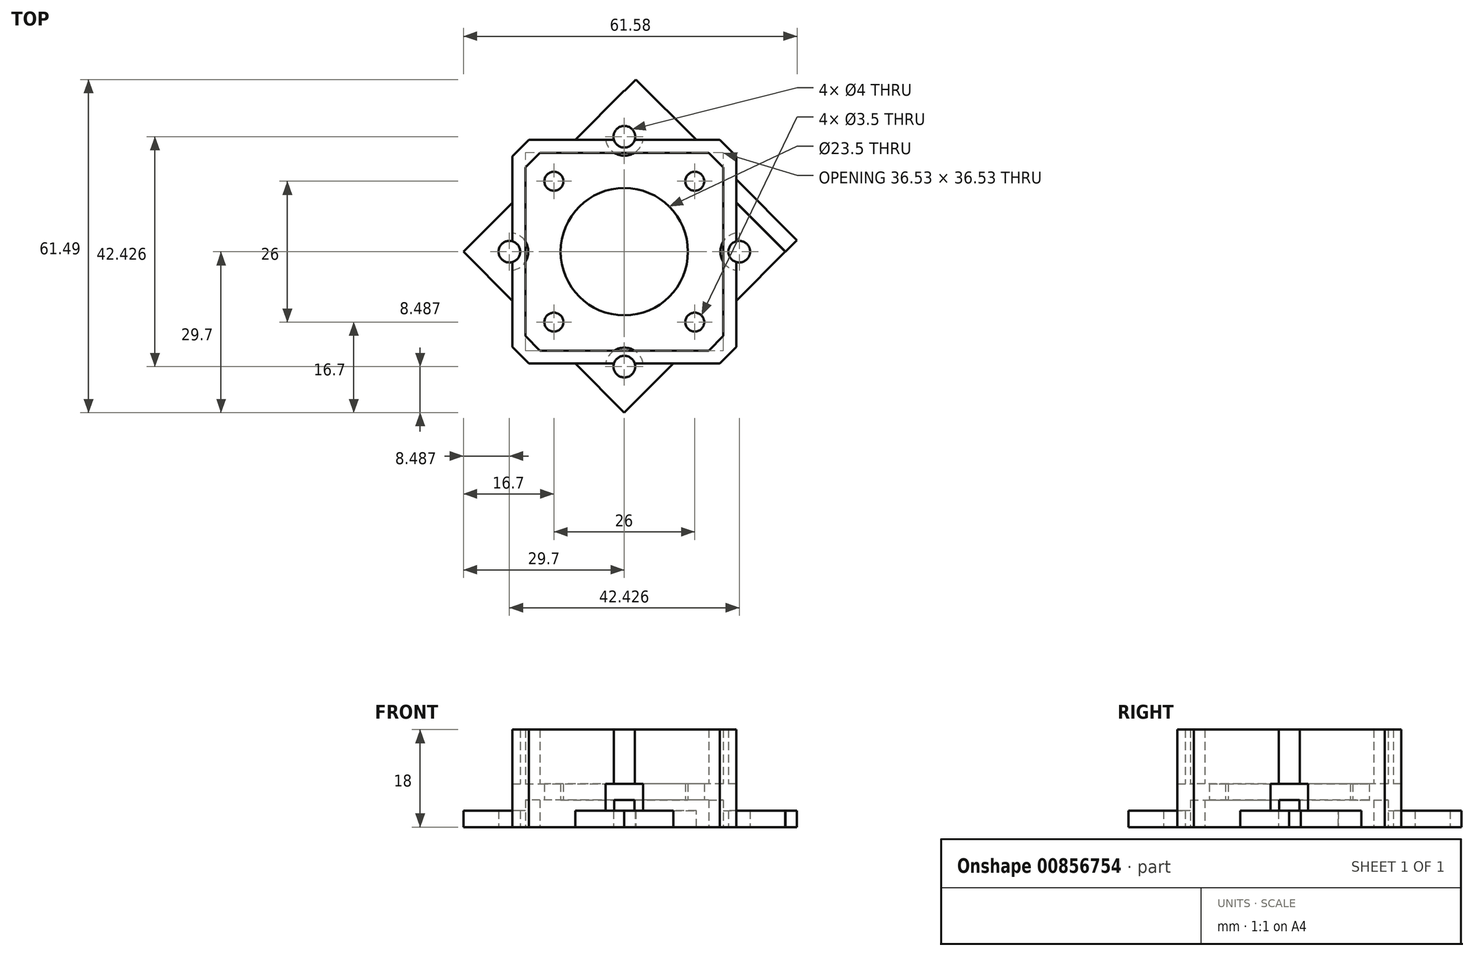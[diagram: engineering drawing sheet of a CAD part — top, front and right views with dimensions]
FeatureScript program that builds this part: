
annotation { "Feature Type Name" : "Feature", "Feature Type Description" : "" }
export const myFeature = defineFeature(function(context is Context, id is Id, definition is map)
    precondition{}
    {
        {
            var Q0;
            Q0=qCreatedBy(makeId("Top.planeOp"),FACE);
            var sketch = newSketch(context, id + "F0", { "sketchPlane" : qUnion([Q0])});
            skLineSegment(sketch, "E0", {"start": v(0, 0) * mm, "end": v(-17.6, 15) * mm});
            skLineSegment(sketch, "E1", {"start": v(0, 0) * mm, "end": v(-15, 17.6) * mm});
            skLineSegment(sketch, "E2", {"start": v(0, 0) * mm, "end": v(-17.6, -15) * mm});
            skLineSegment(sketch, "E3", {"start": v(0, 0) * mm, "end": v(-15, -17.6) * mm});
            skLineSegment(sketch, "E4", {"start": v(0, 0) * mm, "end": v(15, 17.6) * mm});
            skLineSegment(sketch, "E5", {"start": v(0, 0) * mm, "end": v(17.6, 15) * mm});
            skLineSegment(sketch, "E6", {"start": v(0, 0) * mm, "end": v(15, -17.6) * mm});
            skLineSegment(sketch, "E7", {"start": v(0, 0) * mm, "end": v(17.6, -15) * mm});
            skLineSegment(sketch, "E8", {"start": v(0, 0) * mm, "end": v(15.57, 18.27) * mm});
            skLineSegment(sketch, "E9", {"start": v(0, 0) * mm, "end": v(18.27, 15.57) * mm});
            skLineSegment(sketch, "E10", {"start": v(0, 0) * mm, "end": v(18.27, -15.57) * mm});
            skLineSegment(sketch, "E11", {"start": v(0, 0) * mm, "end": v(15.57, -18.27) * mm});
            skLineSegment(sketch, "E12", {"start": v(0, 0) * mm, "end": v(-15.57, -18.27) * mm});
            skLineSegment(sketch, "E13", {"start": v(0, 0) * mm, "end": v(-18.27, -15.57) * mm});
            skLineSegment(sketch, "E14", {"start": v(0, 0) * mm, "end": v(-15.57, 18.27) * mm});
            skLineSegment(sketch, "E15", {"start": v(0, 0) * mm, "end": v(-18.27, 15.57) * mm});
            skLineSegment(sketch, "E16", {"start": v(0, 0) * mm, "end": v(17.6, 20.65) * mm});
            skLineSegment(sketch, "E17", {"start": v(17.6, 20.65) * mm, "end": v(0, 0) * mm});
            skLineSegment(sketch, "E18", {"start": v(0, 0) * mm, "end": v(20.65, 17.6) * mm});
            skLineSegment(sketch, "E19", {"start": v(0, 0) * mm, "end": v(20.65, -17.6) * mm});
            skLineSegment(sketch, "E20", {"start": v(0, 0) * mm, "end": v(17.6, -20.65) * mm});
            skLineSegment(sketch, "E21", {"start": v(0, 0) * mm, "end": v(-17.6, -20.65) * mm});
            skLineSegment(sketch, "E22", {"start": v(0, 0) * mm, "end": v(-20.65, -17.6) * mm});
            skLineSegment(sketch, "E23", {"start": v(0, 0) * mm, "end": v(-20.65, 17.6) * mm});
            skLineSegment(sketch, "E24", {"start": v(0, 0) * mm, "end": v(-17.6, 20.65) * mm});
            skSolve(sketch);
        }
        {
            var Q0;
            Q0=qCreatedBy(makeId("Top.planeOp"),FACE);
            var sketch = newSketch(context, id + "F1", { "sketchPlane" : qUnion([Q0])});
            skLineSegment(sketch, "E25", {"start": v(-18.27, -15.57) * mm, "end": v(-18.27, 15.57) * mm});
            skLineSegment(sketch, "E26", {"start": v(-18.27, 15.57) * mm, "end": v(-15.57, 18.27) * mm});
            skLineSegment(sketch, "E27", {"start": v(-15.57, 18.27) * mm, "end": v(15.57, 18.27) * mm});
            skLineSegment(sketch, "E28", {"start": v(15.57, 18.27) * mm, "end": v(18.27, 15.57) * mm});
            skLineSegment(sketch, "E29", {"start": v(18.27, 15.57) * mm, "end": v(18.27, -15.57) * mm});
            skLineSegment(sketch, "E30", {"start": v(18.27, -15.57) * mm, "end": v(15.57, -18.27) * mm});
            skLineSegment(sketch, "E31", {"start": v(15.57, -18.27) * mm, "end": v(-15.57, -18.27) * mm});
            skLineSegment(sketch, "E32", {"start": v(-15.57, -18.27) * mm, "end": v(-18.27, -15.57) * mm});
            skLineSegment(sketch, "E33", {"start": v(-20.65, 17.6) * mm, "end": v(-20.65, -17.6) * mm});
            skLineSegment(sketch, "E34", {"start": v(-20.65, -17.6) * mm, "end": v(-17.6, -20.65) * mm});
            skLineSegment(sketch, "E35", {"start": v(-17.6, -20.65) * mm, "end": v(17.6, -20.65) * mm});
            skLineSegment(sketch, "E36", {"start": v(17.6, -20.65) * mm, "end": v(20.65, -17.6) * mm});
            skLineSegment(sketch, "E37", {"start": v(20.65, -17.6) * mm, "end": v(20.65, 17.6) * mm});
            skLineSegment(sketch, "E38", {"start": v(20.65, 17.6) * mm, "end": v(17.6, 20.65) * mm});
            skLineSegment(sketch, "E39", {"start": v(17.6, 20.65) * mm, "end": v(-17.6, 20.65) * mm});
            skLineSegment(sketch, "E40", {"start": v(-17.6, 20.65) * mm, "end": v(-20.65, 17.6) * mm});
            skSolve(sketch);
        }
        {
            var Q0;
            Q0=qCreatedBy(makeId("Top.planeOp"),FACE);
            var sketch = newSketch(context, id + "F2", { "sketchPlane" : qUnion([Q0])});
            skCircle(sketch, "E41", {"center": v(0, 0) * mm, "radius": 11.75 * mm});
            skCircle(sketch, "E42", {"center": v(13, 13) * mm, "radius": 1.75 * mm});
            skCircle(sketch, "E43.MirrorC", {"center": v(-13, -13) * mm, "radius": 1.75 * mm});
            skCircle(sketch, "E44.MirrorC", {"center": v(13, -13) * mm, "radius": 1.75 * mm});
            skLineSegment(sketch, "E45", {"start": v(-18.27, 15.57) * mm, "end": v(-15.57, 18.27) * mm});
            skLineSegment(sketch, "E46", {"start": v(-15.57, 18.27) * mm, "end": v(15.57, 18.27) * mm});
            skLineSegment(sketch, "E47", {"start": v(15.57, 18.27) * mm, "end": v(18.27, 15.57) * mm});
            skLineSegment(sketch, "E48", {"start": v(18.27, 15.57) * mm, "end": v(18.27, -15.57) * mm});
            skLineSegment(sketch, "E49", {"start": v(18.27, -15.57) * mm, "end": v(15.57, -18.27) * mm});
            skLineSegment(sketch, "E50", {"start": v(15.57, -18.27) * mm, "end": v(-15.57, -18.27) * mm});
            skLineSegment(sketch, "E51", {"start": v(-15.57, -18.27) * mm, "end": v(-18.27, -15.57) * mm});
            skLineSegment(sketch, "E52", {"start": v(-18.27, -15.57) * mm, "end": v(-18.27, 15.57) * mm});
            skCircle(sketch, "E53.MirrorC", {"center": v(-13, 13) * mm, "radius": 1.75 * mm});
            skSolve(sketch);
        }
        {
            var Q0;
            Q0=qCreatedBy(makeId("Top.planeOp"),FACE);
            var sketch = newSketch(context, id + "F3", { "sketchPlane" : qUnion([Q0])});
            skLineSegment(sketch, "E54.bottom", {"start": v(0, -29.7) * mm, "end": v(-29.7, 0) * mm});
            skLineSegment(sketch, "E54.top", {"start": v(29.7, 0) * mm, "end": v(0, 29.7) * mm});
            skLineSegment(sketch, "E54.left", {"start": v(0, -29.7) * mm, "end": v(29.7, 0) * mm});
            skLineSegment(sketch, "E54.right", {"start": v(-29.7, 0) * mm, "end": v(0, 29.7) * mm});
            skPoint(sketch, "E54.middle", {"position": v(0, 0) * mm});
            skCircle(sketch, "E55", {"center": v(0, 0) * mm, "radius": 11.75 * mm});
            skCircle(sketch, "E56", {"center": v(0, 21.21) * mm, "radius": 2 * mm});
            skCircle(sketch, "E57", {"center": v(21.21, 0) * mm, "radius": 2 * mm});
            skCircle(sketch, "E58", {"center": v(-21.21, 0) * mm, "radius": 2 * mm});
            skCircle(sketch, "E59", {"center": v(0, -21.21) * mm, "radius": 2 * mm});
            skLineSegment(sketch, "E60.bottom", {"start": v(0, 21.21) * mm, "end": v(21.21, 0) * mm, "construction": true});
            skLineSegment(sketch, "E60.top", {"start": v(-21.21, 0) * mm, "end": v(0, -21.21) * mm, "construction": true});
            skLineSegment(sketch, "E60.left", {"start": v(0, 21.21) * mm, "end": v(-21.21, 0) * mm, "construction": true});
            skLineSegment(sketch, "E60.right", {"start": v(21.21, 0) * mm, "end": v(0, -21.21) * mm, "construction": true});
            skCircle(sketch, "E61", {"center": v(-13, 13) * mm, "radius": 1.75 * mm});
            skCircle(sketch, "E62", {"center": v(-13, -13) * mm, "radius": 1.75 * mm});
            skCircle(sketch, "E63", {"center": v(13, -13) * mm, "radius": 1.75 * mm});
            skCircle(sketch, "E64", {"center": v(13, 13) * mm, "radius": 1.75 * mm});
            skSolve(sketch);
        }
        {
            var Q0;
            Q0=makeQuery(id+"F1.imprint","IMPRINT",FACE,{"disambiguationData":[TD([[makeQuery(id+"F1.imprint","IMPRINT",EDGE,{"derivedFrom":sQuery(id+"F1.wireOp",EDGE,"E25")}),1.0]])]});
            extrude(context, id + "F4", {"entities" : qUnion([Q0]), "depth" : 18 * mm, "offsetDistance" : 25 * mm});
        }
        {
            var Q0;
            Q0=makeQuery(id+"F2.imprint","IMPRINT",FACE,{"disambiguationData":[TD([[makeQuery(id+"F2.imprint","IMPRINT",EDGE,{"derivedFrom":sQuery(id+"F2.wireOp",EDGE,"E41")}),-1.0]])]});
            extrude(context, id + "F5", {"entities" : qUnion([Q0]), "operationType" : NewBodyOperationType.ADD, "depth" : 8 * mm, "offsetDistance" : 25 * mm});
        }
        {
            var Q0;
            Q0=makeQuery(id+"F3.imprint","IMPRINT",FACE,{"disambiguationData":[TD([[makeQuery(id+"F3.imprint","IMPRINT",EDGE,{"derivedFrom":sQuery(id+"F3.wireOp",EDGE,"E54.bottom")}),-1.0]])]});
            extrude(context, id + "F6", {"entities" : qUnion([Q0]), "operationType" : NewBodyOperationType.ADD, "depth" : 3 * mm, "offsetDistance" : 25 * mm});
        }
        {
            var Q0;
            Q0=makeQuery(id+"F3.imprint","IMPRINT",FACE,{"disambiguationData":[TD([[makeQuery(id+"F3.imprint","IMPRINT",EDGE,{"derivedFrom":sQuery(id+"F3.wireOp",EDGE,"E57")}),1.0]])]});
            var Q1;
            Q1=makeQuery(id+"F3.imprint","IMPRINT",FACE,{"disambiguationData":[TD([[makeQuery(id+"F3.imprint","IMPRINT",EDGE,{"derivedFrom":sQuery(id+"F3.wireOp",EDGE,"E56")}),1.0]])]});
            var Q2;
            Q2=makeQuery(id+"F3.imprint","IMPRINT",FACE,{"disambiguationData":[TD([[makeQuery(id+"F3.imprint","IMPRINT",EDGE,{"derivedFrom":sQuery(id+"F3.wireOp",EDGE,"E59")}),1.0]])]});
            var Q3;
            Q3=makeQuery(id+"F3.imprint","IMPRINT",FACE,{"disambiguationData":[TD([[makeQuery(id+"F3.imprint","IMPRINT",EDGE,{"derivedFrom":sQuery(id+"F3.wireOp",EDGE,"E58")}),1.0]])]});
            extrude(context, id + "F7", {"entities" : qUnion([Q0, Q1, Q2, Q3]), "operationType" : NewBodyOperationType.REMOVE, "oppositeDirection" : true, "depth" : -18 * mm, "offsetDistance" : 25 * mm});
        }
        {
            var Q0;
            Q0=makeQuery(id+"F6.boolean.opBoolean","MERGE",FACE,{"derivedFrom":[makeQuery(id+"F5.boolean.opBoolean","MERGE",FACE,{"derivedFrom":[makeQuery(id+"F4.opExtrude","CAP_FACE",FACE,{"disambiguationData":[OSD([sQuery(id+"F1.wireOp",EDGE,"E25"),sQuery(id+"F1.wireOp",EDGE,"E26"),sQuery(id+"F1.wireOp",EDGE,"E27"),sQuery(id+"F1.wireOp",EDGE,"E28"),sQuery(id+"F1.wireOp",EDGE,"E29"),sQuery(id+"F1.wireOp",EDGE,"E30"),sQuery(id+"F1.wireOp",EDGE,"E31"),sQuery(id+"F1.wireOp",EDGE,"E32"),sQuery(id+"F1.wireOp",EDGE,"E33"),sQuery(id+"F1.wireOp",EDGE,"E34"),sQuery(id+"F1.wireOp",EDGE,"E35"),sQuery(id+"F1.wireOp",EDGE,"E36"),sQuery(id+"F1.wireOp",EDGE,"E37"),sQuery(id+"F1.wireOp",EDGE,"E38"),sQuery(id+"F1.wireOp",EDGE,"E39"),sQuery(id+"F1.wireOp",EDGE,"E40")])],"isStart":true}),makeQuery(id+"F5.opExtrude","CAP_FACE",FACE,{"disambiguationData":[OSD([sQuery(id+"F2.wireOp",EDGE,"E41"),sQuery(id+"F2.wireOp",EDGE,"E42"),sQuery(id+"F2.wireOp",EDGE,"E43.MirrorC"),sQuery(id+"F2.wireOp",EDGE,"E44.MirrorC"),sQuery(id+"F2.wireOp",EDGE,"E45"),sQuery(id+"F2.wireOp",EDGE,"E46"),sQuery(id+"F2.wireOp",EDGE,"E47"),sQuery(id+"F2.wireOp",EDGE,"E48"),sQuery(id+"F2.wireOp",EDGE,"E49"),sQuery(id+"F2.wireOp",EDGE,"E50"),sQuery(id+"F2.wireOp",EDGE,"E51"),sQuery(id+"F2.wireOp",EDGE,"E52"),sQuery(id+"F2.wireOp",EDGE,"E53.MirrorC")])],"isStart":true})]}),makeQuery(id+"F6.opExtrude","CAP_FACE",FACE,{"disambiguationData":[OSD([sQuery(id+"F3.wireOp",EDGE,"E54.bottom"),sQuery(id+"F3.wireOp",EDGE,"E54.top"),sQuery(id+"F3.wireOp",EDGE,"E54.left"),sQuery(id+"F3.wireOp",EDGE,"E54.right"),sQuery(id+"F3.wireOp",EDGE,"E55"),sQuery(id+"F3.wireOp",EDGE,"E56"),sQuery(id+"F3.wireOp",EDGE,"E57"),sQuery(id+"F3.wireOp",EDGE,"E58"),sQuery(id+"F3.wireOp",EDGE,"E59"),sQuery(id+"F3.wireOp",EDGE,"E61"),sQuery(id+"F3.wireOp",EDGE,"E62"),sQuery(id+"F3.wireOp",EDGE,"E63"),sQuery(id+"F3.wireOp",EDGE,"E64")])],"isStart":true})]});
            var sketch = newSketch(context, id + "F8", { "sketchPlane" : qUnion([Q0])});
            skCircle(sketch, "E65", {"center": v(13, 13) * mm, "radius": 4.5 * mm});
            skCircle(sketch, "E66", {"center": v(-13, -13) * mm, "radius": 4.5 * mm});
            skCircle(sketch, "E67", {"center": v(13, -13) * mm, "radius": 4.5 * mm});
            skCircle(sketch, "E68", {"center": v(-13, 13) * mm, "radius": 4.5 * mm});
            skSolve(sketch);
        }
        {
            var Q0;
            Q0=makeQuery(id+"F8.imprint","IMPRINT",FACE,{"disambiguationData":[TD([[makeQuery(id+"F8.imprint","IMPRINT",EDGE,{"derivedFrom":sQuery(id+"F8.wireOp",EDGE,"E66")}),1.0]])]});
            var Q1;
            Q1=makeQuery(id+"F2.imprint","IMPRINT",FACE,{"disambiguationData":[TD([[makeQuery(id+"F2.imprint","IMPRINT",EDGE,{"derivedFrom":sQuery(id+"F2.wireOp",EDGE,"E53.MirrorC")}),-1.0]])]});
            extrude(context, id + "F9", {"entities" : qUnion([Q0, Q1]), "operationType" : NewBodyOperationType.REMOVE, "oppositeDirection" : true, "depth" : 5 * mm, "offsetDistance" : 25 * mm});
        }
        {
            var Q0;
            Q0=makeQuery(id+"F8.imprint","IMPRINT",FACE,{"disambiguationData":[TD([[makeQuery(id+"F8.imprint","IMPRINT",EDGE,{"derivedFrom":sQuery(id+"F8.wireOp",EDGE,"E65")}),1.0]])]});
            var Q1;
            Q1=makeQuery(id+"F2.imprint","IMPRINT",FACE,{"disambiguationData":[TD([[makeQuery(id+"F2.imprint","IMPRINT",EDGE,{"derivedFrom":sQuery(id+"F2.wireOp",EDGE,"E44.MirrorC")}),-1.0]])]});
            extrude(context, id + "F10", {"entities" : qUnion([Q0, Q1]), "operationType" : NewBodyOperationType.REMOVE, "oppositeDirection" : true, "depth" : 5 * mm, "offsetDistance" : 25 * mm});
        }
        {
            var Q0;
            {var subQ0=sQuery(id+"F3.wireOp",EDGE,"E54.top");var subQ1=sQuery(id+"F3.wireOp",EDGE,"E54.right");var subQ2=sQuery(id+"F3.wireOp",EDGE,"E56");Q0=makeQuery(id+"F6.boolean.opBoolean","SPLIT",FACE,{"disambiguationData":[TD([makeQuery(id+"F4.opExtrude","SWEPT_FACE",FACE,{"disambiguationData":[OSD([sQuery(id+"F1.wireOp",EDGE,"E39")])]})])],"derivedFrom":makeQuery(id+"F6.opExtrude","CAP_FACE",FACE,{"disambiguationData":[OSD([sQuery(id+"F3.wireOp",EDGE,"E54.bottom"),subQ0,sQuery(id+"F3.wireOp",EDGE,"E54.left"),subQ1,sQuery(id+"F3.wireOp",EDGE,"E55"),subQ2,sQuery(id+"F3.wireOp",EDGE,"E57"),sQuery(id+"F3.wireOp",EDGE,"E58"),sQuery(id+"F3.wireOp",EDGE,"E59"),sQuery(id+"F3.wireOp",EDGE,"E61"),sQuery(id+"F3.wireOp",EDGE,"E62"),sQuery(id+"F3.wireOp",EDGE,"E63"),sQuery(id+"F3.wireOp",EDGE,"E64")])],"isStart":false})});}
            var sketch = newSketch(context, id + "F11", { "sketchPlane" : qUnion([Q0])});
            skCircle(sketch, "E69", {"center": v(0, 21.21) * mm, "radius": 3.5 * mm});
            skCircle(sketch, "E70", {"center": v(0, -21.21) * mm, "radius": 3.5 * mm});
            skCircle(sketch, "E71", {"center": v(21.21, 0) * mm, "radius": 3.5 * mm});
            skCircle(sketch, "E72", {"center": v(-21.21, 0) * mm, "radius": 3.5 * mm});
            skSolve(sketch);
        }
        {
            var Q0;
            Q0 = qSketchRegion(id + "F11", true);
            extrude(context, id + "F12", {"entities" : qUnion([Q0]), "operationType" : NewBodyOperationType.REMOVE, "oppositeDirection" : true, "depth" : -5 * mm, "offsetDistance" : 25 * mm});
        }
        {
            var Q0;
            Q0=makeQuery(id+"F3.imprint","IMPRINT",FACE,{"disambiguationData":[TD([[makeQuery(id+"F3.imprint","IMPRINT",EDGE,{"derivedFrom":sQuery(id+"F3.wireOp",EDGE,"E54.bottom")}),-1.0]])]});
            var sketch = newSketch(context, id + "F13", { "sketchPlane" : qUnion([Q0])});
            skLineSegment(sketch, "E73", {"start": v(0, 29.64) * mm, "end": v(4.3, 33.94) * mm});
            skLineSegment(sketch, "E74", {"start": v(29.75, 0) * mm, "end": v(34, 4.25) * mm});
            skLineSegment(sketch, "E75", {"start": v(17.6, 20.65) * mm, "end": v(4.3, 33.94) * mm});
            skLineSegment(sketch, "E76", {"start": v(20.65, 17.6) * mm, "end": v(34, 4.25) * mm});
            skLineSegment(sketch, "E77", {"start": v(2.15, 31.79) * mm, "end": v(31.88, 2.12) * mm});
            skLineSegment(sketch, "E78", {"start": v(0, 29.64) * mm, "end": v(29.75, 0) * mm});
            skLineSegment(sketch, "E79", {"start": v(13.46, 20.5) * mm, "end": v(9.17, 20.5) * mm});
            skLineSegment(sketch, "E80", {"start": v(20.48, 13.5) * mm, "end": v(20.48, 9.24) * mm});
            skLineSegment(sketch, "E81", {"start": v(13.46, 20.5) * mm, "end": v(17.6, 20.65) * mm});
            skLineSegment(sketch, "E82", {"start": v(20.48, 13.5) * mm, "end": v(20.65, 17.6) * mm});
            skLineSegment(sketch, "E83", {"start": v(20.65, 17.6) * mm, "end": v(45.4, -7.15) * mm});
            skLineSegment(sketch, "E84", {"start": v(17.6, 20.65) * mm, "end": v(-7.15, 45.4) * mm});
            skLineSegment(sketch, "E85", {"start": v(-7.15, 45.4) * mm, "end": v(-9.3, 43.24) * mm});
            skLineSegment(sketch, "E86", {"start": v(2.15, 31.79) * mm, "end": v(-9.3, 43.24) * mm});
            skLineSegment(sketch, "E87", {"start": v(31.88, 2.12) * mm, "end": v(43.27, -9.27) * mm});
            skLineSegment(sketch, "E88", {"start": v(45.4, -7.15) * mm, "end": v(43.27, -9.27) * mm});
            skSolve(sketch);
        }
        {
            var Q0;
            {var subQ0=sQuery(id+"F13.wireOp",EDGE,"E77");var subQ1=sQuery(id+"F13.wireOp",EDGE,"E73");var subQ2=makeQuery(id+"F13.imprint","INTERSECT",VERTEX,{"derivedFrom":[subQ1,subQ0]});Q0=makeQuery(id+"F13.imprint","IMPRINT",FACE,{"disambiguationData":[TD([[makeQuery(id+"F13.imprint","IMPRINT",EDGE,{"disambiguationData":[TD([[subQ2,1.0]])],"derivedFrom":subQ1}),-1.0]])]});}
            var Q1;
            {var subQ5=sQuery(id+"F13.wireOp",EDGE,"E80");Q1=makeQuery(id+"F13.imprint","IMPRINT",FACE,{"disambiguationData":[TD([[makeQuery(id+"F13.imprint","IMPRINT",EDGE,{"derivedFrom":subQ5}),1.0]])]});}
            extrude(context, id + "F14", {"entities" : qUnion([Q0, Q1]), "operationType" : NewBodyOperationType.ADD, "depth" : 3 * mm, "offsetDistance" : 25 * mm});
        }
        {
            var Q0;
            Q0=makeQuery(id+"F8.imprint","IMPRINT",FACE,{"disambiguationData":[TD([[makeQuery(id+"F8.imprint","IMPRINT",EDGE,{"derivedFrom":sQuery(id+"F8.wireOp",EDGE,"E67")}),1.0]])]});
            extrude(context, id + "F15", {"entities" : qUnion([Q0]), "operationType" : NewBodyOperationType.REMOVE, "oppositeDirection" : true, "depth" : 5 * mm, "offsetDistance" : 25 * mm});
        }
        {
            var Q0;
            Q0=makeQuery(id+"F8.imprint","IMPRINT",FACE,{"disambiguationData":[TD([[makeQuery(id+"F8.imprint","IMPRINT",EDGE,{"derivedFrom":sQuery(id+"F8.wireOp",EDGE,"E68")}),1.0]])]});
            extrude(context, id + "F16", {"entities" : qUnion([Q0]), "operationType" : NewBodyOperationType.REMOVE, "oppositeDirection" : true, "depth" : 5 * mm, "offsetDistance" : 25 * mm});
        }
        {
            var Q0;
            Q0=makeQuery(id+"FBqxjdhl6pFCTmG_1.boolean.opBoolean","MERGE",FACE,{"derivedFrom":[makeQuery(id+"F4.opExtrude","SWEPT_FACE",FACE,{"disambiguationData":[OSD([sQuery(id+"F1.wireOp",EDGE,"E38")])]}),makeQuery(id+"FBqxjdhl6pFCTmG_1.opExtrude","SWEPT_FACE",FACE,{"disambiguationData":[OSD([sQuery(id+"F13.wireOp",EDGE,"E83")])]}),makeQuery(id+"FBqxjdhl6pFCTmG_1.opExtrude","SWEPT_FACE",FACE,{"disambiguationData":[OSD([sQuery(id+"F13.wireOp",EDGE,"E84")])]})]});
            var sketch = newSketch(context, id + "F17", { "sketchPlane" : qUnion([Q0])});
            skLineSegment(sketch, "E89", {"start": v(37.16, 3.2) * mm, "end": v(33.16, 3.2) * mm});
            skCircle(sketch, "E90", {"center": v(33.16, 3.2) * mm, "radius": 1.75 * mm});
            skLineSegment(sketch, "E91", {"start": v(0, 0) * mm, "end": v(0, 18) * mm});
            skLineSegment(sketch, "E92", {"start": v(37.16, 10) * mm, "end": v(-37.16, 10) * mm});
            skCircle(sketch, "E93.MirrorC", {"center": v(33.16, 16.8) * mm, "radius": 1.75 * mm});
            skCircle(sketch, "E94.MirrorC", {"center": v(-33.16, 16.8) * mm, "radius": 1.75 * mm});
            skCircle(sketch, "E95.MirrorC", {"center": v(-33.16, 3.2) * mm, "radius": 1.75 * mm});
            skSolve(sketch);
        }
        {
            var Q0;
            Q0 = qSketchRegion(id + "F17", true);
            extrude(context, id + "F18", {"entities" : qUnion([Q0]), "operationType" : NewBodyOperationType.REMOVE, "oppositeDirection" : true, "depth" : 5 * mm, "offsetDistance" : 25 * mm});
        }
    });
